# Revit family: LAMP_PUZZLE TR FRAME PROFILE
name_source: partatom
category: Modelos genéricos
revit_build: Autodesk Revit 2015 (Build: 20140606_1530(x64)
units: mm (PartAtom-declared; Revit-internal decimal feet)

## types (4) — shared parameters
Accessory Type = Assembly
Elevación por defecto = 1219 mm
Fabricante = LAMP
Installation instructions = http://www.lamp.es
Last update = 25/07/2018
Manufacturer URL = http://www.lamp.es
Manufacturer country = Spain
Manufacturer name = LAMP
Product datasheet = http://www.lamp.es

## per-type parameters (varying)
| type | Descripción | Dimensions | Distancia | Finish | Material marco | Modelo | Product code | Weight |
| 1M BLACK | PUZZLE ACC. HIDDEN FRAME PROFILE 1M BK. | 1 m | 1000 mm  [stored 3.28084 ft] | Shiny black | LAMP_Aluminio frame Puzzle BL | PUTRFRPR1000B | PUTRFRPR1000B | 0.38 kg |
| 1M WHITE | PUZZLE ACC. HIDDEN FRAME PROFILE 1M WH. | 1 m | 1000 mm  [stored 3.28084 ft] | Shiny white | LAMP_Aluminio frame Puzzle WH | PUTRFRPR1000W | PUTRFRPR1000W | 0.38 kg |
| 3M BLACK | PUZZLE ACC. HIDDEN FRAME PROFILE 3M BK. | 3 m | 3000 mm  [stored 9.84252 ft] | Shiny black | LAMP_Aluminio frame Puzzle BL | PUTRFRPR3000B | PUTRFRPR3000B | 1.15 kg |
| 3M WHITE | PUZZLE ACC. HIDDEN FRAME PROFILE 3M WH. | 3 m | 3000 mm  [stored 9.84252 ft] | Shiny white | LAMP_Aluminio frame Puzzle WH | PUTRFRPR3000W | PUTRFRPR3000W | 1.15 kg |

note: [stored X ft] marks values corroborated as IEEE doubles in the binary element streams (Revit-internal decimal feet)
